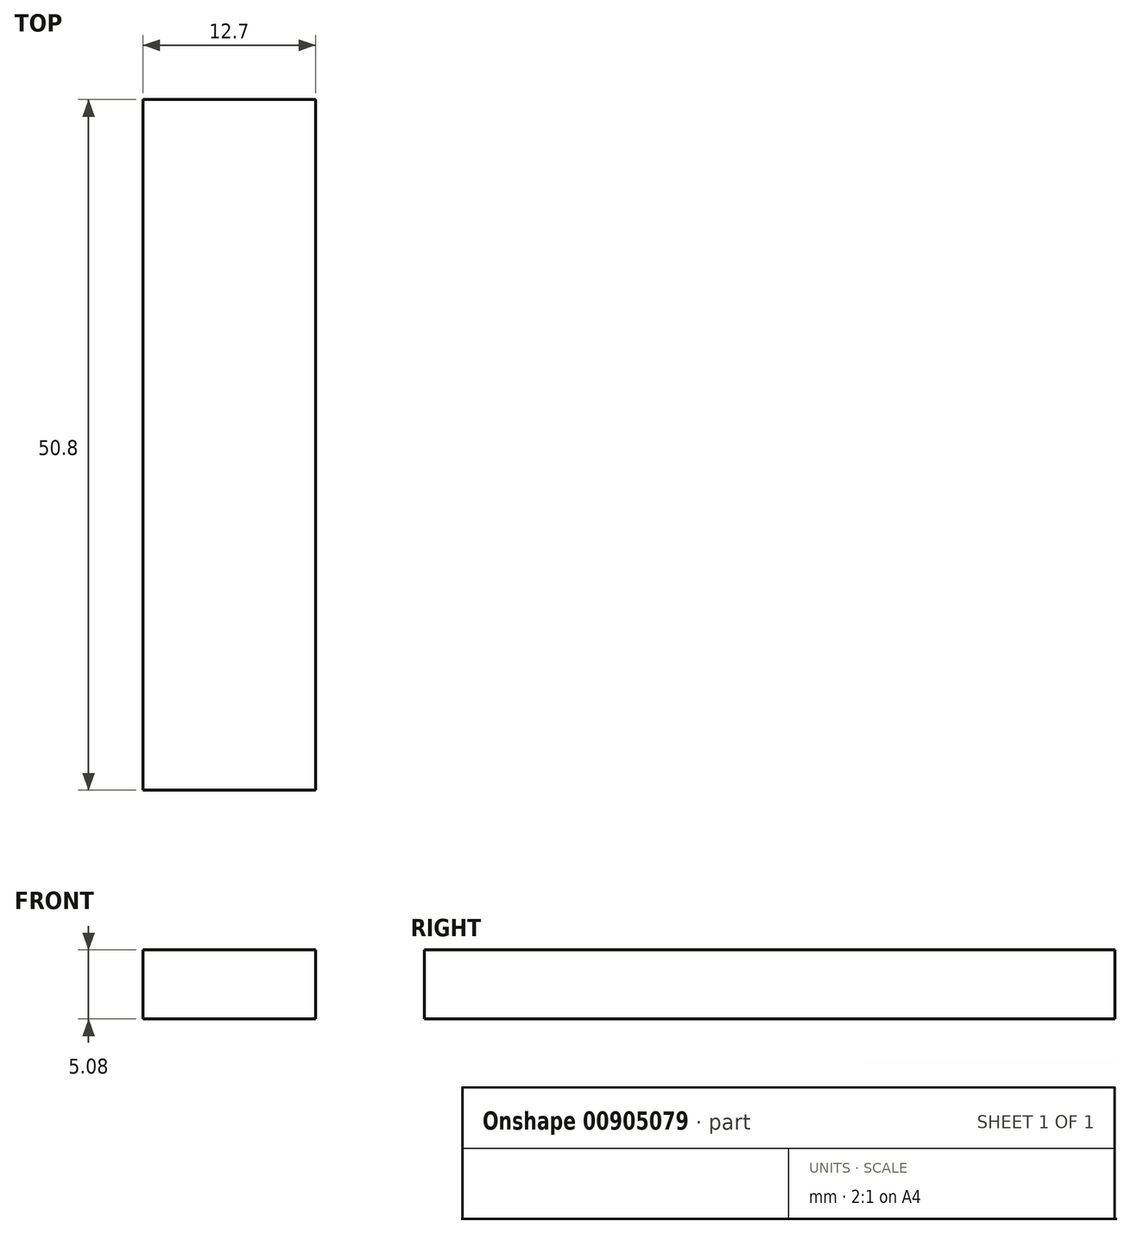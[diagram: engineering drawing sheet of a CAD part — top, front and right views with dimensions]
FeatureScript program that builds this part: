
annotation { "Feature Type Name" : "Feature", "Feature Type Description" : "" }
export const myFeature = defineFeature(function(context is Context, id is Id, definition is map)
    precondition{}
    {
        {
            var Q0;
            Q0=qCreatedBy(makeId("Top.planeOp"),FACE);
            var sketch = newSketch(context, id + "F0", { "sketchPlane" : qUnion([Q0])});
            skLineSegment(sketch, "E0.bottom", {"start": v(6.35, 25.4) * mm, "end": v(-6.35, 25.4) * mm});
            skLineSegment(sketch, "E0.top", {"start": v(6.35, -25.4) * mm, "end": v(-6.35, -25.4) * mm});
            skLineSegment(sketch, "E0.left", {"start": v(6.35, 25.4) * mm, "end": v(6.35, -25.4) * mm});
            skLineSegment(sketch, "E0.right", {"start": v(-6.35, 25.4) * mm, "end": v(-6.35, -25.4) * mm});
            skPoint(sketch, "E0.middle", {"position": v(0, 0) * mm});
            skSolve(sketch);
        }
        {
            var Q0;
            Q0=makeQuery(id+"F0.imprint","IMPRINT",FACE,{"disambiguationData":[TD([[makeQuery(id+"F0.imprint","IMPRINT",EDGE,{"derivedFrom":sQuery(id+"F0.wireOp",EDGE,"E0.bottom")}),1.0]])]});
            extrude(context, id + "F1", {"entities" : qUnion([Q0]), "depth" : 5.08 * mm, "offsetDistance" : 25.4 * mm});
        }
    });
